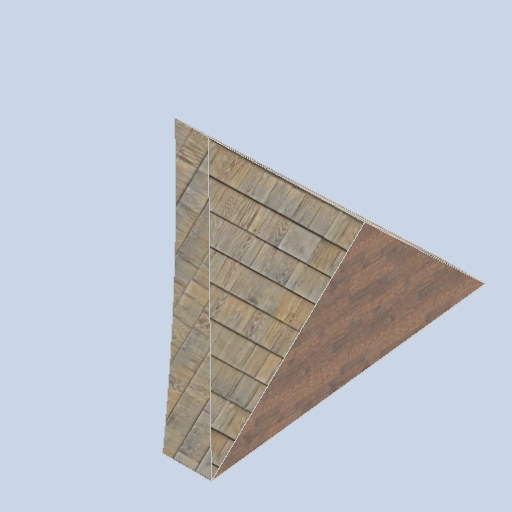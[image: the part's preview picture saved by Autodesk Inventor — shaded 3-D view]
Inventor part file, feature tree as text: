
AUTODESK INVENTOR PART (.ipt)
format: ipt  version: 2024.2 (Build 282272000, 272)  size: 302,592 bytes
history: native  units: in
note: dims shown in document units (in); Inventor stores cm internally (conversion verified against a paired STEP export)
features: sketch x7, plane x6, other x3
ambient origin geometry x8: Origin, YZ Plane, XZ Plane, XY Plane, X Axis, Y Axis, Z Axis, Center Point
bodies: Solid1 (feature_tree)
feature tree (16):
  other  "panel_pad_02 _MIR.ipt"
  other  "Solid1::panel_pad_02 _MIR.ipt"
  other  "TaggingFeature1"
  sketch  "Sketch1"  dims[d0=0.3937in]
  sketch  "Sketch2"
  sketch  "Sketch3"
  sketch  "Sketch6"
  sketch  "Sketch7"
  sketch  "Sketch8"
  sketch  "Sketch9"
  plane  "Work Plane1"
  plane  "Work Plane2"
  plane  "Work Plane3"
  plane  "Work Plane4"
  plane  "Work Plane5"
  plane  "Work Plane6"
